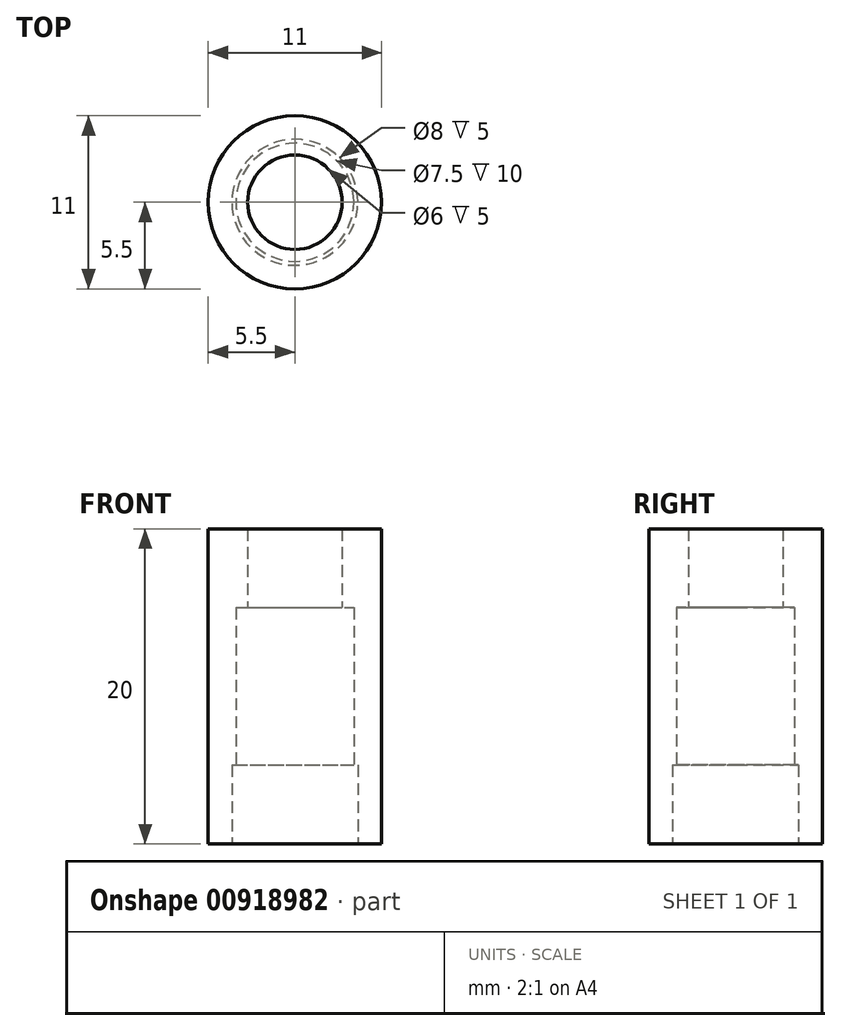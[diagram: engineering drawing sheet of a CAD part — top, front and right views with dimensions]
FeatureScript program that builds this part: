
annotation { "Feature Type Name" : "Feature", "Feature Type Description" : "" }
export const myFeature = defineFeature(function(context is Context, id is Id, definition is map)
    precondition{}
    {
        {
            var Q0;
            Q0=qCreatedBy(makeId("Front.planeOp"),FACE);
            var sketch = newSketch(context, id + "F0", { "sketchPlane" : qUnion([Q0])});
            skLineSegment(sketch, "E0", {"start": v(0, 0) * mm, "end": v(1.5, 0) * mm});
            skLineSegment(sketch, "E1", {"start": v(1.5, 0) * mm, "end": v(1.5, 5) * mm});
            skLineSegment(sketch, "E2", {"start": v(1.75, 5) * mm, "end": v(1.5, 5) * mm});
            skLineSegment(sketch, "E3", {"start": v(1.75, 5) * mm, "end": v(1.75, 15) * mm});
            skLineSegment(sketch, "E4", {"start": v(2.5, 15) * mm, "end": v(1.75, 15) * mm});
            skLineSegment(sketch, "E5", {"start": v(2.5, 15) * mm, "end": v(2.5, 20) * mm});
            skLineSegment(sketch, "E6", {"start": v(2.5, 20) * mm, "end": v(0, 20) * mm});
            skLineSegment(sketch, "E7", {"start": v(0, 20) * mm, "end": v(0, 0) * mm});
            skLineSegment(sketch, "E8", {"start": v(5.5, 0) * mm, "end": v(5.5, 20) * mm, "construction": true});
            skSolve(sketch);
        }
        {
            var Q0;
            Q0=makeQuery(id+"F0.imprint","IMPRINT",FACE,{"disambiguationData":[TD([[makeQuery(id+"F0.imprint","IMPRINT",EDGE,{"derivedFrom":sQuery(id+"F0.wireOp",EDGE,"E0")}),1.0]])]});
            var Q1;
            Q1=sQuery(id+"F0.wireOp",EDGE,"E8");
            revolve(context, id + "F1", {"surfaceOperationType" : NewSurfaceOperationType.NEW, "entities" : qUnion([Q0]), "axis" : qUnion([Q1]), "revolveType" : RevolveType.FULL});
        }
    });
